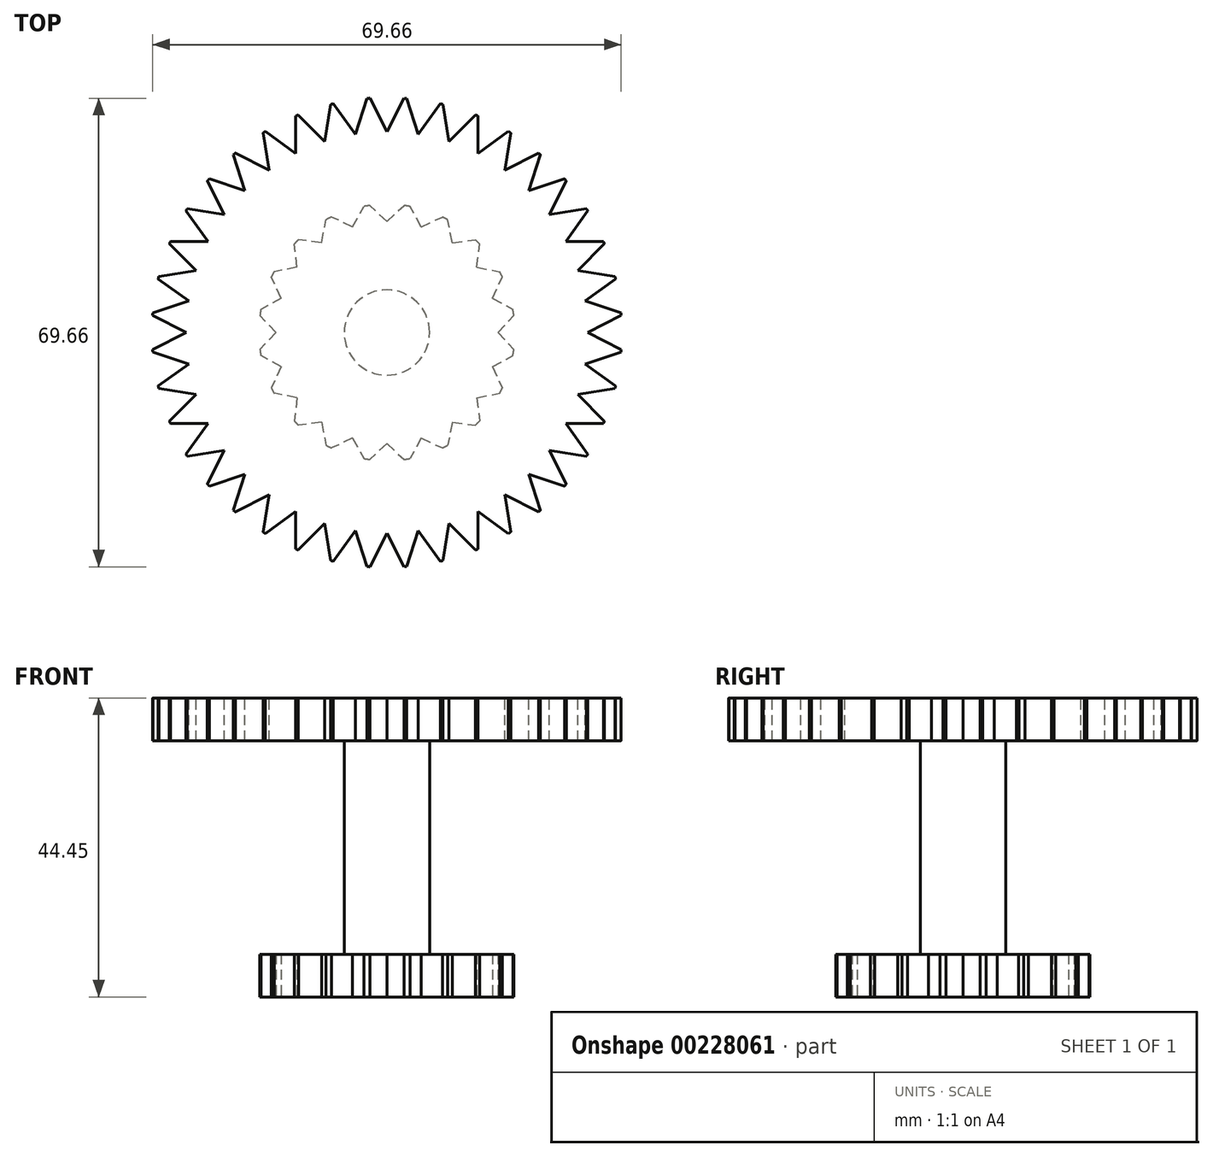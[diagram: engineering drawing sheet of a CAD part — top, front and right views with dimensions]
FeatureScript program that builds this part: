
annotation { "Feature Type Name" : "Feature", "Feature Type Description" : "" }
export const myFeature = defineFeature(function(context is Context, id is Id, definition is map)
    precondition{}
    {
        {
            var Q0;
            Q0=qCreatedBy(makeId("Top.planeOp"),FACE);
            var sketch = newSketch(context, id + "F0", { "sketchPlane" : qUnion([Q0])});
            skCircle(sketch, "E0", {"center": v(0, 0) * mm, "radius": 19.05 * mm});
            skSolve(sketch);
        }
        {
            var Q0;
            Q0 = qSketchRegion(id + "F0", true);
            extrude(context, id + "F1", {"entities" : qUnion([Q0]), "depth" : 6.35 * mm, "offsetDistance" : 25.4 * mm});
        }
        {
            var Q0;
            Q0=makeQuery(id+"F1.opExtrude","CAP_FACE",FACE,{"disambiguationData":[OSD([sQuery(id+"F0.wireOp",EDGE,"E0")])],"isStart":false});
            var sketch = newSketch(context, id + "F2", { "sketchPlane" : qUnion([Q0])});
            skCircle(sketch, "E1", {"center": v(0, 0) * mm, "radius": 6.35 * mm});
            skSolve(sketch);
        }
        {
            var Q0;
            Q0 = qSketchRegion(id + "F2", true);
            extrude(context, id + "F3", {"entities" : qUnion([Q0]), "operationType" : NewBodyOperationType.ADD, "depth" : 31.75 * mm, "offsetDistance" : 25.4 * mm});
        }
        {
            var Q0;
            Q0=makeQuery(id+"F3.opExtrude","CAP_FACE",FACE,{"disambiguationData":[OSD([sQuery(id+"F2.wireOp",EDGE,"E1")])],"isStart":false});
            var sketch = newSketch(context, id + "F4", { "sketchPlane" : qUnion([Q0])});
            skCircle(sketch, "E2", {"center": v(0, 0) * mm, "radius": 34.93 * mm});
            skSolve(sketch);
        }
        {
            var Q0;
            Q0 = qSketchRegion(id + "F4", true);
            extrude(context, id + "F5", {"entities" : qUnion([Q0]), "operationType" : NewBodyOperationType.ADD, "depth" : 6.35 * mm, "offsetDistance" : 25.4 * mm});
        }
        {
            var Q0;
            Q0=makeQuery(id+"F1.opExtrude","CAP_FACE",FACE,{"disambiguationData":[OSD([sQuery(id+"F0.wireOp",EDGE,"E0")])],"isStart":true});
            var sketch = newSketch(context, id + "F6", { "sketchPlane" : qUnion([Q0])});
            skLineSegment(sketch, "E3", {"start": v(0, 16.51) * mm, "end": v(2.54, 18.88) * mm});
            skLineSegment(sketch, "E4", {"start": v(0, 16.51) * mm, "end": v(0, 19.05) * mm, "construction": true});
            skLineSegment(sketch, "E5", {"start": v(0, 16.51) * mm, "end": v(-2.54, 18.88) * mm});
            skArc(sketch, "E6", {"start": v(2.54, 18.88) * mm, "mid": v(0, 19.05) * mm, "end": v(-2.54, 18.88) * mm});
            skLineSegment(sketch, "E7.1.0", {"start": v(-5.1, 15.7) * mm, "end": v(-5.89, 18.12) * mm, "construction": true});
            skLineSegment(sketch, "E7.1.1", {"start": v(-5.1, 15.7) * mm, "end": v(-8.25, 17.17) * mm});
            skArc(sketch, "E7.1.2", {"start": v(-3.42, 18.74) * mm, "mid": v(-5.89, 18.12) * mm, "end": v(-8.25, 17.17) * mm});
            skLineSegment(sketch, "E7.1.3", {"start": v(-5.1, 15.7) * mm, "end": v(-3.42, 18.74) * mm});
            skLineSegment(sketch, "E7.2.0", {"start": v(-9.7, 13.36) * mm, "end": v(-11.2, 15.41) * mm, "construction": true});
            skLineSegment(sketch, "E7.2.1", {"start": v(-9.7, 13.36) * mm, "end": v(-13.15, 13.78) * mm});
            skArc(sketch, "E7.2.2", {"start": v(-9.04, 16.77) * mm, "mid": v(-11.2, 15.41) * mm, "end": v(-13.15, 13.78) * mm});
            skLineSegment(sketch, "E7.2.3", {"start": v(-9.7, 13.36) * mm, "end": v(-9.04, 16.77) * mm});
            skLineSegment(sketch, "E7.3.0", {"start": v(-13.36, 9.7) * mm, "end": v(-15.41, 11.2) * mm, "construction": true});
            skLineSegment(sketch, "E7.3.1", {"start": v(-13.36, 9.7) * mm, "end": v(-16.77, 9.04) * mm});
            skArc(sketch, "E7.3.2", {"start": v(-13.78, 13.15) * mm, "mid": v(-15.41, 11.2) * mm, "end": v(-16.77, 9.04) * mm});
            skLineSegment(sketch, "E7.3.3", {"start": v(-13.36, 9.7) * mm, "end": v(-13.78, 13.15) * mm});
            skLineSegment(sketch, "E7.4.0", {"start": v(-15.7, 5.1) * mm, "end": v(-18.12, 5.89) * mm, "construction": true});
            skLineSegment(sketch, "E7.4.1", {"start": v(-15.7, 5.1) * mm, "end": v(-18.74, 3.42) * mm});
            skArc(sketch, "E7.4.2", {"start": v(-17.17, 8.25) * mm, "mid": v(-18.12, 5.89) * mm, "end": v(-18.74, 3.42) * mm});
            skLineSegment(sketch, "E7.4.3", {"start": v(-15.7, 5.1) * mm, "end": v(-17.17, 8.25) * mm});
            skLineSegment(sketch, "E7.5.0", {"start": v(-16.51, 0) * mm, "end": v(-19.05, 0) * mm, "construction": true});
            skLineSegment(sketch, "E7.5.1", {"start": v(-16.51, 0) * mm, "end": v(-18.88, -2.54) * mm});
            skArc(sketch, "E7.5.2", {"start": v(-18.88, 2.54) * mm, "mid": v(-19.05, 0) * mm, "end": v(-18.88, -2.54) * mm});
            skLineSegment(sketch, "E7.5.3", {"start": v(-16.51, 0) * mm, "end": v(-18.88, 2.54) * mm});
            skLineSegment(sketch, "E7.6.0", {"start": v(-15.7, -5.1) * mm, "end": v(-18.12, -5.89) * mm, "construction": true});
            skLineSegment(sketch, "E7.6.1", {"start": v(-15.7, -5.1) * mm, "end": v(-17.17, -8.25) * mm});
            skArc(sketch, "E7.6.2", {"start": v(-18.74, -3.42) * mm, "mid": v(-18.12, -5.89) * mm, "end": v(-17.17, -8.25) * mm});
            skLineSegment(sketch, "E7.6.3", {"start": v(-15.7, -5.1) * mm, "end": v(-18.74, -3.42) * mm});
            skLineSegment(sketch, "E7.7.0", {"start": v(-13.36, -9.7) * mm, "end": v(-15.41, -11.2) * mm, "construction": true});
            skLineSegment(sketch, "E7.7.1", {"start": v(-13.36, -9.7) * mm, "end": v(-13.78, -13.15) * mm});
            skArc(sketch, "E7.7.2", {"start": v(-16.77, -9.04) * mm, "mid": v(-15.41, -11.2) * mm, "end": v(-13.78, -13.15) * mm});
            skLineSegment(sketch, "E7.7.3", {"start": v(-13.36, -9.7) * mm, "end": v(-16.77, -9.04) * mm});
            skLineSegment(sketch, "E7.8.0", {"start": v(-9.7, -13.36) * mm, "end": v(-11.2, -15.41) * mm, "construction": true});
            skLineSegment(sketch, "E7.8.1", {"start": v(-9.7, -13.36) * mm, "end": v(-9.04, -16.77) * mm});
            skArc(sketch, "E7.8.2", {"start": v(-13.15, -13.78) * mm, "mid": v(-11.2, -15.41) * mm, "end": v(-9.04, -16.77) * mm});
            skLineSegment(sketch, "E7.8.3", {"start": v(-9.7, -13.36) * mm, "end": v(-13.15, -13.78) * mm});
            skLineSegment(sketch, "E7.9.0", {"start": v(-5.1, -15.7) * mm, "end": v(-5.89, -18.12) * mm, "construction": true});
            skLineSegment(sketch, "E7.9.1", {"start": v(-5.1, -15.7) * mm, "end": v(-3.42, -18.74) * mm});
            skArc(sketch, "E7.9.2", {"start": v(-8.25, -17.17) * mm, "mid": v(-5.89, -18.12) * mm, "end": v(-3.42, -18.74) * mm});
            skLineSegment(sketch, "E7.9.3", {"start": v(-5.1, -15.7) * mm, "end": v(-8.25, -17.17) * mm});
            skLineSegment(sketch, "E7.10.0", {"start": v(0, -16.51) * mm, "end": v(0, -19.05) * mm, "construction": true});
            skLineSegment(sketch, "E7.10.1", {"start": v(0, -16.51) * mm, "end": v(2.54, -18.88) * mm});
            skArc(sketch, "E7.10.2", {"start": v(-2.54, -18.88) * mm, "mid": v(0, -19.05) * mm, "end": v(2.54, -18.88) * mm});
            skLineSegment(sketch, "E7.10.3", {"start": v(0, -16.51) * mm, "end": v(-2.54, -18.88) * mm});
            skLineSegment(sketch, "E7.11.0", {"start": v(5.1, -15.7) * mm, "end": v(5.89, -18.12) * mm, "construction": true});
            skLineSegment(sketch, "E7.11.1", {"start": v(5.1, -15.7) * mm, "end": v(8.25, -17.17) * mm});
            skArc(sketch, "E7.11.2", {"start": v(3.42, -18.74) * mm, "mid": v(5.89, -18.12) * mm, "end": v(8.25, -17.17) * mm});
            skLineSegment(sketch, "E7.11.3", {"start": v(5.1, -15.7) * mm, "end": v(3.42, -18.74) * mm});
            skLineSegment(sketch, "E7.12.0", {"start": v(9.7, -13.36) * mm, "end": v(11.2, -15.41) * mm, "construction": true});
            skLineSegment(sketch, "E7.12.1", {"start": v(9.7, -13.36) * mm, "end": v(13.15, -13.78) * mm});
            skArc(sketch, "E7.12.2", {"start": v(9.04, -16.77) * mm, "mid": v(11.2, -15.41) * mm, "end": v(13.15, -13.78) * mm});
            skLineSegment(sketch, "E7.12.3", {"start": v(9.7, -13.36) * mm, "end": v(9.04, -16.77) * mm});
            skLineSegment(sketch, "E7.13.0", {"start": v(13.36, -9.7) * mm, "end": v(15.41, -11.2) * mm, "construction": true});
            skLineSegment(sketch, "E7.13.1", {"start": v(13.36, -9.7) * mm, "end": v(16.77, -9.04) * mm});
            skArc(sketch, "E7.13.2", {"start": v(13.78, -13.15) * mm, "mid": v(15.41, -11.2) * mm, "end": v(16.77, -9.04) * mm});
            skLineSegment(sketch, "E7.13.3", {"start": v(13.36, -9.7) * mm, "end": v(13.78, -13.15) * mm});
            skLineSegment(sketch, "E7.14.0", {"start": v(15.7, -5.1) * mm, "end": v(18.12, -5.89) * mm, "construction": true});
            skLineSegment(sketch, "E7.14.1", {"start": v(15.7, -5.1) * mm, "end": v(18.74, -3.42) * mm});
            skArc(sketch, "E7.14.2", {"start": v(17.17, -8.25) * mm, "mid": v(18.12, -5.89) * mm, "end": v(18.74, -3.42) * mm});
            skLineSegment(sketch, "E7.14.3", {"start": v(15.7, -5.1) * mm, "end": v(17.17, -8.25) * mm});
            skLineSegment(sketch, "E7.15.0", {"start": v(16.51, 0) * mm, "end": v(19.05, 0) * mm, "construction": true});
            skLineSegment(sketch, "E7.15.1", {"start": v(16.51, 0) * mm, "end": v(18.88, 2.54) * mm});
            skArc(sketch, "E7.15.2", {"start": v(18.88, -2.54) * mm, "mid": v(19.05, 0) * mm, "end": v(18.88, 2.54) * mm});
            skLineSegment(sketch, "E7.15.3", {"start": v(16.51, 0) * mm, "end": v(18.88, -2.54) * mm});
            skLineSegment(sketch, "E7.16.0", {"start": v(15.7, 5.1) * mm, "end": v(18.12, 5.89) * mm, "construction": true});
            skLineSegment(sketch, "E7.16.1", {"start": v(15.7, 5.1) * mm, "end": v(17.17, 8.25) * mm});
            skArc(sketch, "E7.16.2", {"start": v(18.74, 3.42) * mm, "mid": v(18.12, 5.89) * mm, "end": v(17.17, 8.25) * mm});
            skLineSegment(sketch, "E7.16.3", {"start": v(15.7, 5.1) * mm, "end": v(18.74, 3.42) * mm});
            skLineSegment(sketch, "E7.17.0", {"start": v(13.36, 9.7) * mm, "end": v(15.41, 11.2) * mm, "construction": true});
            skLineSegment(sketch, "E7.17.1", {"start": v(13.36, 9.7) * mm, "end": v(13.78, 13.15) * mm});
            skArc(sketch, "E7.17.2", {"start": v(16.77, 9.04) * mm, "mid": v(15.41, 11.2) * mm, "end": v(13.78, 13.15) * mm});
            skLineSegment(sketch, "E7.17.3", {"start": v(13.36, 9.7) * mm, "end": v(16.77, 9.04) * mm});
            skLineSegment(sketch, "E7.18.0", {"start": v(9.7, 13.36) * mm, "end": v(11.2, 15.41) * mm, "construction": true});
            skLineSegment(sketch, "E7.18.1", {"start": v(9.7, 13.36) * mm, "end": v(9.04, 16.77) * mm});
            skArc(sketch, "E7.18.2", {"start": v(13.15, 13.78) * mm, "mid": v(11.2, 15.41) * mm, "end": v(9.04, 16.77) * mm});
            skLineSegment(sketch, "E7.18.3", {"start": v(9.7, 13.36) * mm, "end": v(13.15, 13.78) * mm});
            skLineSegment(sketch, "E7.19.0", {"start": v(5.1, 15.7) * mm, "end": v(5.89, 18.12) * mm, "construction": true});
            skLineSegment(sketch, "E7.19.1", {"start": v(5.1, 15.7) * mm, "end": v(3.42, 18.74) * mm});
            skArc(sketch, "E7.19.2", {"start": v(8.25, 17.17) * mm, "mid": v(5.89, 18.12) * mm, "end": v(3.42, 18.74) * mm});
            skLineSegment(sketch, "E7.19.3", {"start": v(5.1, 15.7) * mm, "end": v(8.25, 17.17) * mm});
            skSolve(sketch);
        }
        {
            var Q0;
            Q0 = qSketchRegion(id + "F6", true);
            extrude(context, id + "F7", {"entities" : qUnion([Q0]), "operationType" : NewBodyOperationType.REMOVE, "oppositeDirection" : true, "depth" : 25.4 * mm, "offsetDistance" : 25.4 * mm});
        }
        {
            var Q0;
            Q0=makeQuery(id+"F5.opExtrude","CAP_FACE",FACE,{"disambiguationData":[OSD([sQuery(id+"F4.wireOp",EDGE,"E2")])],"isStart":false});
            var sketch = newSketch(context, id + "F8", { "sketchPlane" : qUnion([Q0])});
            skLineSegment(sketch, "E8", {"start": v(0, 34.93) * mm, "end": v(0, 29.85) * mm, "construction": true});
            skLineSegment(sketch, "E9", {"start": v(0, 29.85) * mm, "end": v(2.54, 34.83) * mm});
            skLineSegment(sketch, "E10", {"start": v(0, 29.85) * mm, "end": v(-2.54, 34.83) * mm});
            skArc(sketch, "E11", {"start": v(2.54, 34.83) * mm, "mid": v(0, 34.93) * mm, "end": v(-2.54, 34.83) * mm});
            skLineSegment(sketch, "E12.1.0", {"start": v(-4.67, 29.48) * mm, "end": v(-2.94, 34.8) * mm});
            skLineSegment(sketch, "E12.1.1", {"start": v(-4.67, 29.48) * mm, "end": v(-7.96, 34) * mm});
            skLineSegment(sketch, "E12.1.2", {"start": v(-5.46, 34.5) * mm, "end": v(-4.67, 29.48) * mm, "construction": true});
            skArc(sketch, "E12.1.3", {"start": v(-2.94, 34.8) * mm, "mid": v(-5.46, 34.5) * mm, "end": v(-7.96, 34) * mm});
            skLineSegment(sketch, "E12.2.0", {"start": v(-9.22, 28.38) * mm, "end": v(-8.35, 33.91) * mm});
            skLineSegment(sketch, "E12.2.1", {"start": v(-9.22, 28.38) * mm, "end": v(-13.18, 32.34) * mm});
            skLineSegment(sketch, "E12.2.2", {"start": v(-10.8, 33.22) * mm, "end": v(-9.22, 28.38) * mm, "construction": true});
            skArc(sketch, "E12.2.3", {"start": v(-8.35, 33.91) * mm, "mid": v(-10.8, 33.22) * mm, "end": v(-13.18, 32.34) * mm});
            skLineSegment(sketch, "E12.3.0", {"start": v(-13.55, 26.6) * mm, "end": v(-13.55, 32.19) * mm});
            skLineSegment(sketch, "E12.3.1", {"start": v(-13.55, 26.6) * mm, "end": v(-18.08, 29.88) * mm});
            skLineSegment(sketch, "E12.3.2", {"start": v(-15.86, 31.12) * mm, "end": v(-13.55, 26.6) * mm, "construction": true});
            skArc(sketch, "E12.3.3", {"start": v(-13.55, 32.19) * mm, "mid": v(-15.86, 31.12) * mm, "end": v(-18.08, 29.88) * mm});
            skLineSegment(sketch, "E12.4.0", {"start": v(-17.54, 24.15) * mm, "end": v(-18.42, 29.67) * mm});
            skLineSegment(sketch, "E12.4.1", {"start": v(-17.54, 24.15) * mm, "end": v(-22.53, 26.69) * mm});
            skLineSegment(sketch, "E12.4.2", {"start": v(-20.53, 28.25) * mm, "end": v(-17.54, 24.15) * mm, "construction": true});
            skArc(sketch, "E12.4.3", {"start": v(-18.42, 29.67) * mm, "mid": v(-20.53, 28.25) * mm, "end": v(-22.53, 26.69) * mm});
            skLineSegment(sketch, "E12.5.0", {"start": v(-21.1, 21.1) * mm, "end": v(-22.83, 26.43) * mm});
            skLineSegment(sketch, "E12.5.1", {"start": v(-21.1, 21.1) * mm, "end": v(-26.43, 22.83) * mm});
            skLineSegment(sketch, "E12.5.2", {"start": v(-24.7, 24.7) * mm, "end": v(-21.1, 21.1) * mm, "construction": true});
            skArc(sketch, "E12.5.3", {"start": v(-22.83, 26.43) * mm, "mid": v(-24.7, 24.7) * mm, "end": v(-26.43, 22.83) * mm});
            skLineSegment(sketch, "E12.6.0", {"start": v(-24.15, 17.54) * mm, "end": v(-26.69, 22.53) * mm});
            skLineSegment(sketch, "E12.6.1", {"start": v(-24.15, 17.54) * mm, "end": v(-29.67, 18.42) * mm});
            skLineSegment(sketch, "E12.6.2", {"start": v(-28.25, 20.53) * mm, "end": v(-24.15, 17.54) * mm, "construction": true});
            skArc(sketch, "E12.6.3", {"start": v(-26.69, 22.53) * mm, "mid": v(-28.25, 20.53) * mm, "end": v(-29.67, 18.42) * mm});
            skLineSegment(sketch, "E12.7.0", {"start": v(-26.6, 13.55) * mm, "end": v(-29.88, 18.08) * mm});
            skLineSegment(sketch, "E12.7.1", {"start": v(-26.6, 13.55) * mm, "end": v(-32.19, 13.55) * mm});
            skLineSegment(sketch, "E12.7.2", {"start": v(-31.12, 15.86) * mm, "end": v(-26.6, 13.55) * mm, "construction": true});
            skArc(sketch, "E12.7.3", {"start": v(-29.88, 18.08) * mm, "mid": v(-31.12, 15.86) * mm, "end": v(-32.19, 13.55) * mm});
            skLineSegment(sketch, "E12.8.0", {"start": v(-28.38, 9.22) * mm, "end": v(-32.34, 13.18) * mm});
            skLineSegment(sketch, "E12.8.1", {"start": v(-28.38, 9.22) * mm, "end": v(-33.91, 8.35) * mm});
            skLineSegment(sketch, "E12.8.2", {"start": v(-33.22, 10.8) * mm, "end": v(-28.38, 9.22) * mm, "construction": true});
            skArc(sketch, "E12.8.3", {"start": v(-32.34, 13.18) * mm, "mid": v(-33.22, 10.8) * mm, "end": v(-33.91, 8.35) * mm});
            skLineSegment(sketch, "E12.9.0", {"start": v(-29.48, 4.67) * mm, "end": v(-34, 7.96) * mm});
            skLineSegment(sketch, "E12.9.1", {"start": v(-29.48, 4.67) * mm, "end": v(-34.8, 2.94) * mm});
            skLineSegment(sketch, "E12.9.2", {"start": v(-34.5, 5.46) * mm, "end": v(-29.48, 4.67) * mm, "construction": true});
            skArc(sketch, "E12.9.3", {"start": v(-34, 7.96) * mm, "mid": v(-34.5, 5.46) * mm, "end": v(-34.8, 2.94) * mm});
            skLineSegment(sketch, "E12.10.0", {"start": v(-29.85, 0) * mm, "end": v(-34.83, 2.54) * mm});
            skLineSegment(sketch, "E12.10.1", {"start": v(-29.85, 0) * mm, "end": v(-34.83, -2.54) * mm});
            skLineSegment(sketch, "E12.10.2", {"start": v(-34.93, 0) * mm, "end": v(-29.85, 0) * mm, "construction": true});
            skArc(sketch, "E12.10.3", {"start": v(-34.83, 2.54) * mm, "mid": v(-34.93, 0) * mm, "end": v(-34.83, -2.54) * mm});
            skLineSegment(sketch, "E12.11.0", {"start": v(-29.48, -4.67) * mm, "end": v(-34.8, -2.94) * mm});
            skLineSegment(sketch, "E12.11.1", {"start": v(-29.48, -4.67) * mm, "end": v(-34, -7.96) * mm});
            skLineSegment(sketch, "E12.11.2", {"start": v(-34.5, -5.46) * mm, "end": v(-29.48, -4.67) * mm, "construction": true});
            skArc(sketch, "E12.11.3", {"start": v(-34.8, -2.94) * mm, "mid": v(-34.5, -5.46) * mm, "end": v(-34, -7.96) * mm});
            skLineSegment(sketch, "E12.12.0", {"start": v(-28.38, -9.22) * mm, "end": v(-33.91, -8.35) * mm});
            skLineSegment(sketch, "E12.12.1", {"start": v(-28.38, -9.22) * mm, "end": v(-32.34, -13.18) * mm});
            skLineSegment(sketch, "E12.12.2", {"start": v(-33.22, -10.8) * mm, "end": v(-28.38, -9.22) * mm, "construction": true});
            skArc(sketch, "E12.12.3", {"start": v(-33.91, -8.35) * mm, "mid": v(-33.22, -10.8) * mm, "end": v(-32.34, -13.18) * mm});
            skLineSegment(sketch, "E12.13.0", {"start": v(-26.6, -13.55) * mm, "end": v(-32.19, -13.55) * mm});
            skLineSegment(sketch, "E12.13.1", {"start": v(-26.6, -13.55) * mm, "end": v(-29.88, -18.08) * mm});
            skLineSegment(sketch, "E12.13.2", {"start": v(-31.12, -15.86) * mm, "end": v(-26.6, -13.55) * mm, "construction": true});
            skArc(sketch, "E12.13.3", {"start": v(-32.19, -13.55) * mm, "mid": v(-31.12, -15.86) * mm, "end": v(-29.88, -18.08) * mm});
            skLineSegment(sketch, "E12.14.0", {"start": v(-24.15, -17.54) * mm, "end": v(-29.67, -18.42) * mm});
            skLineSegment(sketch, "E12.14.1", {"start": v(-24.15, -17.54) * mm, "end": v(-26.69, -22.53) * mm});
            skLineSegment(sketch, "E12.14.2", {"start": v(-28.25, -20.53) * mm, "end": v(-24.15, -17.54) * mm, "construction": true});
            skArc(sketch, "E12.14.3", {"start": v(-29.67, -18.42) * mm, "mid": v(-28.25, -20.53) * mm, "end": v(-26.69, -22.53) * mm});
            skLineSegment(sketch, "E12.15.0", {"start": v(-21.1, -21.1) * mm, "end": v(-26.43, -22.83) * mm});
            skLineSegment(sketch, "E12.15.1", {"start": v(-21.1, -21.1) * mm, "end": v(-22.83, -26.43) * mm});
            skLineSegment(sketch, "E12.15.2", {"start": v(-24.7, -24.7) * mm, "end": v(-21.1, -21.1) * mm, "construction": true});
            skArc(sketch, "E12.15.3", {"start": v(-26.43, -22.83) * mm, "mid": v(-24.7, -24.7) * mm, "end": v(-22.83, -26.43) * mm});
            skLineSegment(sketch, "E12.16.0", {"start": v(-17.54, -24.15) * mm, "end": v(-22.53, -26.69) * mm});
            skLineSegment(sketch, "E12.16.1", {"start": v(-17.54, -24.15) * mm, "end": v(-18.42, -29.67) * mm});
            skLineSegment(sketch, "E12.16.2", {"start": v(-20.53, -28.25) * mm, "end": v(-17.54, -24.15) * mm, "construction": true});
            skArc(sketch, "E12.16.3", {"start": v(-22.53, -26.69) * mm, "mid": v(-20.53, -28.25) * mm, "end": v(-18.42, -29.67) * mm});
            skLineSegment(sketch, "E12.17.0", {"start": v(-13.55, -26.6) * mm, "end": v(-18.08, -29.88) * mm});
            skLineSegment(sketch, "E12.17.1", {"start": v(-13.55, -26.6) * mm, "end": v(-13.55, -32.19) * mm});
            skLineSegment(sketch, "E12.17.2", {"start": v(-15.86, -31.12) * mm, "end": v(-13.55, -26.6) * mm, "construction": true});
            skArc(sketch, "E12.17.3", {"start": v(-18.08, -29.88) * mm, "mid": v(-15.86, -31.12) * mm, "end": v(-13.55, -32.19) * mm});
            skLineSegment(sketch, "E12.18.0", {"start": v(-9.22, -28.38) * mm, "end": v(-13.18, -32.34) * mm});
            skLineSegment(sketch, "E12.18.1", {"start": v(-9.22, -28.38) * mm, "end": v(-8.35, -33.91) * mm});
            skLineSegment(sketch, "E12.18.2", {"start": v(-10.8, -33.22) * mm, "end": v(-9.22, -28.38) * mm, "construction": true});
            skArc(sketch, "E12.18.3", {"start": v(-13.18, -32.34) * mm, "mid": v(-10.8, -33.22) * mm, "end": v(-8.35, -33.91) * mm});
            skLineSegment(sketch, "E12.19.0", {"start": v(-4.67, -29.48) * mm, "end": v(-7.96, -34) * mm});
            skLineSegment(sketch, "E12.19.1", {"start": v(-4.67, -29.48) * mm, "end": v(-2.94, -34.8) * mm});
            skLineSegment(sketch, "E12.19.2", {"start": v(-5.46, -34.5) * mm, "end": v(-4.67, -29.48) * mm, "construction": true});
            skArc(sketch, "E12.19.3", {"start": v(-7.96, -34) * mm, "mid": v(-5.46, -34.5) * mm, "end": v(-2.94, -34.8) * mm});
            skLineSegment(sketch, "E12.20.0", {"start": v(0, -29.85) * mm, "end": v(-2.54, -34.83) * mm});
            skLineSegment(sketch, "E12.20.1", {"start": v(0, -29.85) * mm, "end": v(2.54, -34.83) * mm});
            skLineSegment(sketch, "E12.20.2", {"start": v(0, -34.93) * mm, "end": v(0, -29.85) * mm, "construction": true});
            skArc(sketch, "E12.20.3", {"start": v(-2.54, -34.83) * mm, "mid": v(0, -34.93) * mm, "end": v(2.54, -34.83) * mm});
            skLineSegment(sketch, "E12.21.0", {"start": v(4.67, -29.48) * mm, "end": v(2.94, -34.8) * mm});
            skLineSegment(sketch, "E12.21.1", {"start": v(4.67, -29.48) * mm, "end": v(7.96, -34) * mm});
            skLineSegment(sketch, "E12.21.2", {"start": v(5.46, -34.5) * mm, "end": v(4.67, -29.48) * mm, "construction": true});
            skArc(sketch, "E12.21.3", {"start": v(2.94, -34.8) * mm, "mid": v(5.46, -34.5) * mm, "end": v(7.96, -34) * mm});
            skLineSegment(sketch, "E12.22.0", {"start": v(9.22, -28.38) * mm, "end": v(8.35, -33.91) * mm});
            skLineSegment(sketch, "E12.22.1", {"start": v(9.22, -28.38) * mm, "end": v(13.18, -32.34) * mm});
            skLineSegment(sketch, "E12.22.2", {"start": v(10.8, -33.22) * mm, "end": v(9.22, -28.38) * mm, "construction": true});
            skArc(sketch, "E12.22.3", {"start": v(8.35, -33.91) * mm, "mid": v(10.8, -33.22) * mm, "end": v(13.18, -32.34) * mm});
            skLineSegment(sketch, "E12.23.0", {"start": v(13.55, -26.6) * mm, "end": v(13.55, -32.19) * mm});
            skLineSegment(sketch, "E12.23.1", {"start": v(13.55, -26.6) * mm, "end": v(18.08, -29.88) * mm});
            skLineSegment(sketch, "E12.23.2", {"start": v(15.86, -31.12) * mm, "end": v(13.55, -26.6) * mm, "construction": true});
            skArc(sketch, "E12.23.3", {"start": v(13.55, -32.19) * mm, "mid": v(15.86, -31.12) * mm, "end": v(18.08, -29.88) * mm});
            skLineSegment(sketch, "E12.24.0", {"start": v(17.54, -24.15) * mm, "end": v(18.42, -29.67) * mm});
            skLineSegment(sketch, "E12.24.1", {"start": v(17.54, -24.15) * mm, "end": v(22.53, -26.69) * mm});
            skLineSegment(sketch, "E12.24.2", {"start": v(20.53, -28.25) * mm, "end": v(17.54, -24.15) * mm, "construction": true});
            skArc(sketch, "E12.24.3", {"start": v(18.42, -29.67) * mm, "mid": v(20.53, -28.25) * mm, "end": v(22.53, -26.69) * mm});
            skLineSegment(sketch, "E12.25.0", {"start": v(21.1, -21.1) * mm, "end": v(22.83, -26.43) * mm});
            skLineSegment(sketch, "E12.25.1", {"start": v(21.1, -21.1) * mm, "end": v(26.43, -22.83) * mm});
            skLineSegment(sketch, "E12.25.2", {"start": v(24.7, -24.7) * mm, "end": v(21.1, -21.1) * mm, "construction": true});
            skArc(sketch, "E12.25.3", {"start": v(22.83, -26.43) * mm, "mid": v(24.7, -24.7) * mm, "end": v(26.43, -22.83) * mm});
            skLineSegment(sketch, "E12.26.0", {"start": v(24.15, -17.54) * mm, "end": v(26.69, -22.53) * mm});
            skLineSegment(sketch, "E12.26.1", {"start": v(24.15, -17.54) * mm, "end": v(29.67, -18.42) * mm});
            skLineSegment(sketch, "E12.26.2", {"start": v(28.25, -20.53) * mm, "end": v(24.15, -17.54) * mm, "construction": true});
            skArc(sketch, "E12.26.3", {"start": v(26.69, -22.53) * mm, "mid": v(28.25, -20.53) * mm, "end": v(29.67, -18.42) * mm});
            skLineSegment(sketch, "E12.27.0", {"start": v(26.6, -13.55) * mm, "end": v(29.88, -18.08) * mm});
            skLineSegment(sketch, "E12.27.1", {"start": v(26.6, -13.55) * mm, "end": v(32.19, -13.55) * mm});
            skLineSegment(sketch, "E12.27.2", {"start": v(31.12, -15.86) * mm, "end": v(26.6, -13.55) * mm, "construction": true});
            skArc(sketch, "E12.27.3", {"start": v(29.88, -18.08) * mm, "mid": v(31.12, -15.86) * mm, "end": v(32.19, -13.55) * mm});
            skLineSegment(sketch, "E12.28.0", {"start": v(28.38, -9.22) * mm, "end": v(32.34, -13.18) * mm});
            skLineSegment(sketch, "E12.28.1", {"start": v(28.38, -9.22) * mm, "end": v(33.91, -8.35) * mm});
            skLineSegment(sketch, "E12.28.2", {"start": v(33.22, -10.8) * mm, "end": v(28.38, -9.22) * mm, "construction": true});
            skArc(sketch, "E12.28.3", {"start": v(32.34, -13.18) * mm, "mid": v(33.22, -10.8) * mm, "end": v(33.91, -8.35) * mm});
            skLineSegment(sketch, "E12.29.0", {"start": v(29.48, -4.67) * mm, "end": v(34, -7.96) * mm});
            skLineSegment(sketch, "E12.29.1", {"start": v(29.48, -4.67) * mm, "end": v(34.8, -2.94) * mm});
            skLineSegment(sketch, "E12.29.2", {"start": v(34.5, -5.46) * mm, "end": v(29.48, -4.67) * mm, "construction": true});
            skArc(sketch, "E12.29.3", {"start": v(34, -7.96) * mm, "mid": v(34.5, -5.46) * mm, "end": v(34.8, -2.94) * mm});
            skLineSegment(sketch, "E12.30.0", {"start": v(29.85, 0) * mm, "end": v(34.83, -2.54) * mm});
            skLineSegment(sketch, "E12.30.1", {"start": v(29.85, 0) * mm, "end": v(34.83, 2.54) * mm});
            skLineSegment(sketch, "E12.30.2", {"start": v(34.93, 0) * mm, "end": v(29.85, 0) * mm, "construction": true});
            skArc(sketch, "E12.30.3", {"start": v(34.83, -2.54) * mm, "mid": v(34.93, 0) * mm, "end": v(34.83, 2.54) * mm});
            skLineSegment(sketch, "E12.31.0", {"start": v(29.48, 4.67) * mm, "end": v(34.8, 2.94) * mm});
            skLineSegment(sketch, "E12.31.1", {"start": v(29.48, 4.67) * mm, "end": v(34, 7.96) * mm});
            skLineSegment(sketch, "E12.31.2", {"start": v(34.5, 5.46) * mm, "end": v(29.48, 4.67) * mm, "construction": true});
            skArc(sketch, "E12.31.3", {"start": v(34.8, 2.94) * mm, "mid": v(34.5, 5.46) * mm, "end": v(34, 7.96) * mm});
            skLineSegment(sketch, "E12.32.0", {"start": v(28.38, 9.22) * mm, "end": v(33.91, 8.35) * mm});
            skLineSegment(sketch, "E12.32.1", {"start": v(28.38, 9.22) * mm, "end": v(32.34, 13.18) * mm});
            skLineSegment(sketch, "E12.32.2", {"start": v(33.22, 10.8) * mm, "end": v(28.38, 9.22) * mm, "construction": true});
            skArc(sketch, "E12.32.3", {"start": v(33.91, 8.35) * mm, "mid": v(33.22, 10.8) * mm, "end": v(32.34, 13.18) * mm});
            skLineSegment(sketch, "E12.33.0", {"start": v(26.6, 13.55) * mm, "end": v(32.19, 13.55) * mm});
            skLineSegment(sketch, "E12.33.1", {"start": v(26.6, 13.55) * mm, "end": v(29.88, 18.08) * mm});
            skLineSegment(sketch, "E12.33.2", {"start": v(31.12, 15.86) * mm, "end": v(26.6, 13.55) * mm, "construction": true});
            skArc(sketch, "E12.33.3", {"start": v(32.19, 13.55) * mm, "mid": v(31.12, 15.86) * mm, "end": v(29.88, 18.08) * mm});
            skLineSegment(sketch, "E12.34.0", {"start": v(24.15, 17.54) * mm, "end": v(29.67, 18.42) * mm});
            skLineSegment(sketch, "E12.34.1", {"start": v(24.15, 17.54) * mm, "end": v(26.69, 22.53) * mm});
            skLineSegment(sketch, "E12.34.2", {"start": v(28.25, 20.53) * mm, "end": v(24.15, 17.54) * mm, "construction": true});
            skArc(sketch, "E12.34.3", {"start": v(29.67, 18.42) * mm, "mid": v(28.25, 20.53) * mm, "end": v(26.69, 22.53) * mm});
            skLineSegment(sketch, "E12.35.0", {"start": v(21.1, 21.1) * mm, "end": v(26.43, 22.83) * mm});
            skLineSegment(sketch, "E12.35.1", {"start": v(21.1, 21.1) * mm, "end": v(22.83, 26.43) * mm});
            skLineSegment(sketch, "E12.35.2", {"start": v(24.7, 24.7) * mm, "end": v(21.1, 21.1) * mm, "construction": true});
            skArc(sketch, "E12.35.3", {"start": v(26.43, 22.83) * mm, "mid": v(24.7, 24.7) * mm, "end": v(22.83, 26.43) * mm});
            skLineSegment(sketch, "E12.36.0", {"start": v(17.54, 24.15) * mm, "end": v(22.53, 26.69) * mm});
            skLineSegment(sketch, "E12.36.1", {"start": v(17.54, 24.15) * mm, "end": v(18.42, 29.67) * mm});
            skLineSegment(sketch, "E12.36.2", {"start": v(20.53, 28.25) * mm, "end": v(17.54, 24.15) * mm, "construction": true});
            skArc(sketch, "E12.36.3", {"start": v(22.53, 26.69) * mm, "mid": v(20.53, 28.25) * mm, "end": v(18.42, 29.67) * mm});
            skLineSegment(sketch, "E12.37.0", {"start": v(13.55, 26.6) * mm, "end": v(18.08, 29.88) * mm});
            skLineSegment(sketch, "E12.37.1", {"start": v(13.55, 26.6) * mm, "end": v(13.55, 32.19) * mm});
            skLineSegment(sketch, "E12.37.2", {"start": v(15.86, 31.12) * mm, "end": v(13.55, 26.6) * mm, "construction": true});
            skArc(sketch, "E12.37.3", {"start": v(18.08, 29.88) * mm, "mid": v(15.86, 31.12) * mm, "end": v(13.55, 32.19) * mm});
            skLineSegment(sketch, "E12.38.0", {"start": v(9.22, 28.38) * mm, "end": v(13.18, 32.34) * mm});
            skLineSegment(sketch, "E12.38.1", {"start": v(9.22, 28.38) * mm, "end": v(8.35, 33.91) * mm});
            skLineSegment(sketch, "E12.38.2", {"start": v(10.8, 33.22) * mm, "end": v(9.22, 28.38) * mm, "construction": true});
            skArc(sketch, "E12.38.3", {"start": v(13.18, 32.34) * mm, "mid": v(10.8, 33.22) * mm, "end": v(8.35, 33.91) * mm});
            skLineSegment(sketch, "E12.39.0", {"start": v(4.67, 29.48) * mm, "end": v(7.96, 34) * mm});
            skLineSegment(sketch, "E12.39.1", {"start": v(4.67, 29.48) * mm, "end": v(2.94, 34.8) * mm});
            skLineSegment(sketch, "E12.39.2", {"start": v(5.46, 34.5) * mm, "end": v(4.67, 29.48) * mm, "construction": true});
            skArc(sketch, "E12.39.3", {"start": v(7.96, 34) * mm, "mid": v(5.46, 34.5) * mm, "end": v(2.94, 34.8) * mm});
            skSolve(sketch);
        }
        {
            var Q0;
            Q0 = qSketchRegion(id + "F8", true);
            extrude(context, id + "F9", {"entities" : qUnion([Q0]), "operationType" : NewBodyOperationType.REMOVE, "oppositeDirection" : true, "depth" : 25.4 * mm, "offsetDistance" : 25.4 * mm});
        }
    });
